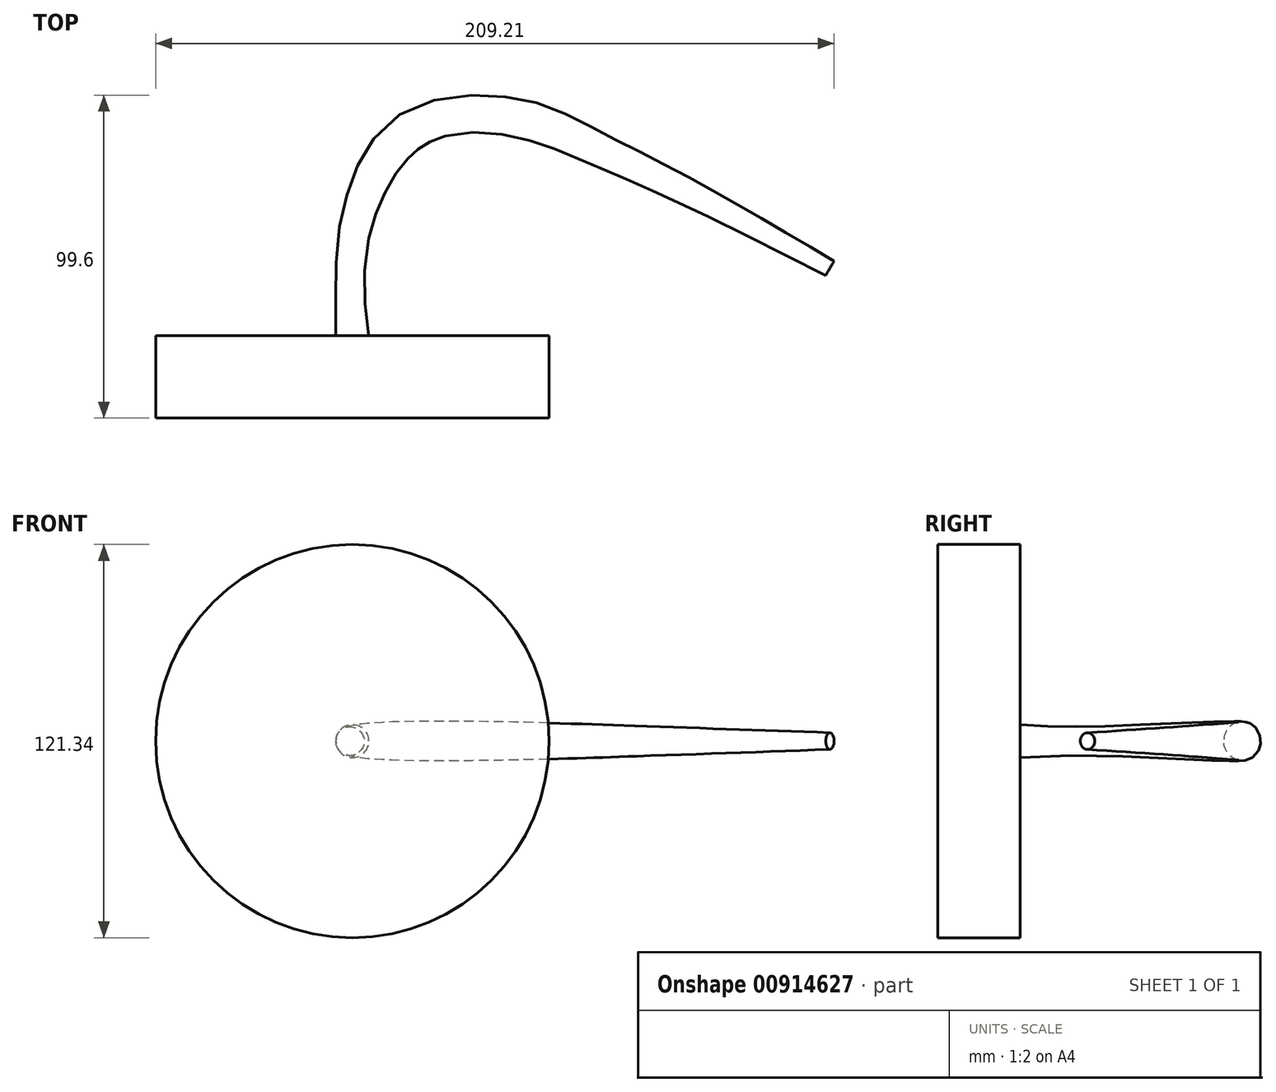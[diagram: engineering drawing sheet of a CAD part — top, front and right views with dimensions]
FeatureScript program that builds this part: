
annotation { "Feature Type Name" : "Feature", "Feature Type Description" : "" }
export const myFeature = defineFeature(function(context is Context, id is Id, definition is map)
    precondition{}
    {
        {
            var Q0;
            Q0=qCreatedBy(makeId("Front.planeOp"),FACE);
            var sketch = newSketch(context, id + "F0", { "sketchPlane" : qUnion([Q0])});
            skCircle(sketch, "E0", {"center": v(0, 0) * mm, "radius": 60.67 * mm});
            skSolve(sketch);
        }
        {
            var Q0;
            Q0 = qSketchRegion(id + "F0", true);
            extrude(context, id + "F1", {"entities" : qUnion([Q0]), "depth" : 25.4 * mm, "offsetDistance" : 25.4 * mm});
        }
        {
            var Q0;
            Q0=qCreatedBy(makeId("Top.planeOp"),FACE);
            var sketch = newSketch(context, id + "F2", { "sketchPlane" : qUnion([Q0])});
            skFitSpline(sketch, "E1", {"points": [v(0, 0) * mm, v(2.73, 38.26) * mm, v(27.18, 67.78) * mm, v(75.9, 57.77) * mm, v(121.4, 35.24) * mm, v(147.3, 20.85) * mm], "startDerivative": vector(-9.42, 197.53) * mm, "endDerivative": vector(142.35, -80.52) * mm});
            skSolve(sketch);
        }
        {
            var Q0;
            Q0=qCreatedBy(makeId("Front.planeOp"),FACE);
            var sketch = newSketch(context, id + "F3", { "sketchPlane" : qUnion([Q0])});
            skCircle(sketch, "E2", {"center": v(0, 0) * mm, "radius": 5.08 * mm});
            skSolve(sketch);
        }
        {
            var Q0;
            Q0=sQuery(id+"F2.wireOp",VERTEX,"E1.end");
            var Q1;
            Q1=sQuery(id+"F2.wireOp",EDGE,"E1");
            cPlane(context, id + "F4", {"entities" : qUnion([Q0, Q1]), "cplaneType" : CPlaneType.CURVE_POINT, "offset" : 25.4 * mm, "width" : 152.4 * mm, "height" : 152.4 * mm});
        }
        {
            var Q0;
            Q0=sQuery(id+"F2.wireOp",VERTEX,"E1.1.internal");
            var Q1;
            Q1=sQuery(id+"F2.wireOp",EDGE,"E1");
            cPlane(context, id + "F5", {"entities" : qUnion([Q0, Q1]), "cplaneType" : CPlaneType.CURVE_POINT, "offset" : 25.4 * mm, "oppositeDirection" : true, "width" : 152.4 * mm, "height" : 152.4 * mm});
        }
        {
            var Q0;
            Q0=qCreatedBy(id+"F5.planeOp",FACE);
            var sketch = newSketch(context, id + "F6", { "sketchPlane" : qUnion([Q0])});
            skCircle(sketch, "E3", {"center": v(9.27, 0) * mm, "radius": 5.08 * mm});
            skSolve(sketch);
        }
        {
            var Q0;
            Q0=sQuery(id+"F2.wireOp",VERTEX,"E1.3.internal");
            var Q1;
            Q1=sQuery(id+"F2.wireOp",EDGE,"E1");
            cPlane(context, id + "F7", {"entities" : qUnion([Q0, Q1]), "cplaneType" : CPlaneType.CURVE_POINT, "offset" : 25.4 * mm, "width" : 152.4 * mm, "height" : 152.4 * mm});
        }
        {
            var Q0;
            Q0=qCreatedBy(id+"F7.planeOp",FACE);
            var sketch = newSketch(context, id + "F8", { "sketchPlane" : qUnion([Q0])});
            skCircle(sketch, "E4", {"center": v(83.33, 0) * mm, "radius": 5.08 * mm});
            skSolve(sketch);
        }
        {
            var Q0;
            Q0=qCreatedBy(id+"F4.planeOp",FACE);
            var sketch = newSketch(context, id + "F9", { "sketchPlane" : qUnion([Q0])});
            skCircle(sketch, "E5", {"center": v(90.62, 0) * mm, "radius": 2.58 * mm});
            skSolve(sketch);
        }
        {
            var Q0;
            Q0=sQuery(id+"F2.wireOp",EDGE,"E1");
            var Q1;
            Q1=makeQuery(id+"F3.imprint","IMPRINT",FACE,{"disambiguationData":[TD([[makeQuery(id+"F3.imprint","IMPRINT",EDGE,{"derivedFrom":sQuery(id+"F3.wireOp",EDGE,"E2")}),1.0]])]});
            var Q2;
            Q2=makeQuery(id+"F6.imprint","IMPRINT",FACE,{"disambiguationData":[TD([[makeQuery(id+"F6.imprint","IMPRINT",EDGE,{"derivedFrom":sQuery(id+"F6.wireOp",EDGE,"E3")}),1.0]])]});
            var Q3;
            Q3=makeQuery(id+"F8.imprint","IMPRINT",FACE,{"disambiguationData":[TD([[makeQuery(id+"F8.imprint","IMPRINT",EDGE,{"derivedFrom":sQuery(id+"F8.wireOp",EDGE,"E4")}),1.0]])]});
            var Q4;
            Q4=makeQuery(id+"F9.imprint","IMPRINT",FACE,{"disambiguationData":[TD([[makeQuery(id+"F9.imprint","IMPRINT",EDGE,{"derivedFrom":sQuery(id+"F9.wireOp",EDGE,"E5")}),1.0]])]});
            loft(context, id + "F10", {"addSections" : true, "spine" : qUnion([Q0]), "sectionCount" : 5, "sheetProfilesArray" : [{ "sheetProfileEntities" : qUnion([Q1]) }, { "sheetProfileEntities" : qUnion([Q2]) }, { "sheetProfileEntities" : qUnion([Q3]) }, { "sheetProfileEntities" : qUnion([Q4]) }]});
        }
    });
